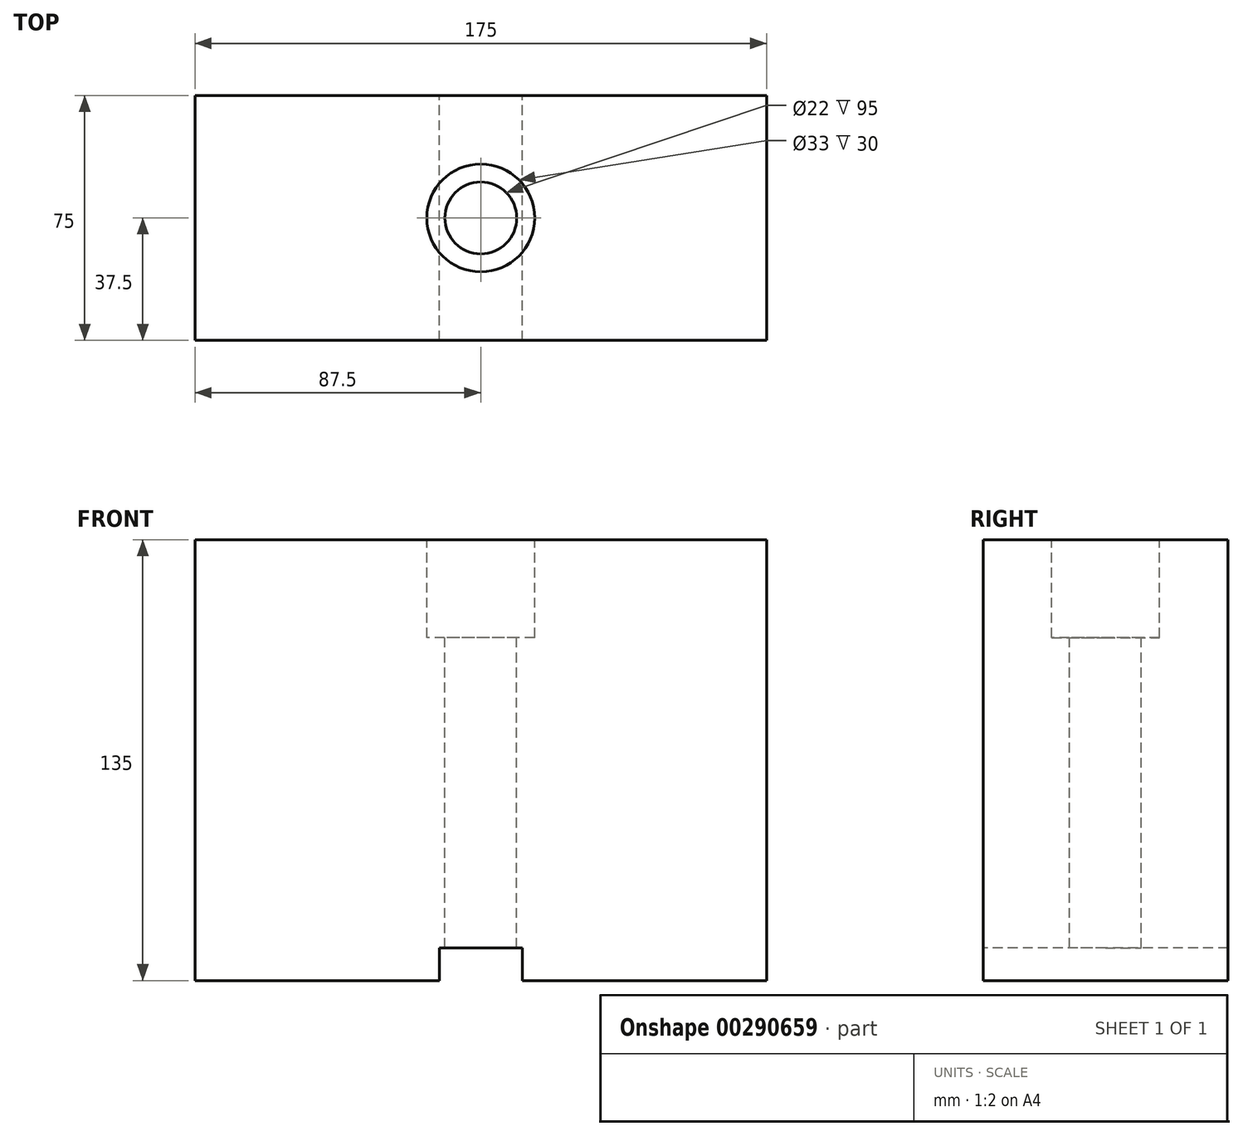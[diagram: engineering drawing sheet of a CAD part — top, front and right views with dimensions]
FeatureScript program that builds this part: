
annotation { "Feature Type Name" : "Feature", "Feature Type Description" : "" }
export const myFeature = defineFeature(function(context is Context, id is Id, definition is map)
    precondition{}
    {
        {
            var Q0;
            Q0=qCreatedBy(makeId("Front.planeOp"),FACE);
            var sketch = newSketch(context, id + "F0", { "sketchPlane" : qUnion([Q0])});
            skLineSegment(sketch, "E0.bottom", {"start": v(0, 0) * mm, "end": v(-175, 0) * mm});
            skLineSegment(sketch, "E0.top", {"start": v(0, 135) * mm, "end": v(-175, 135) * mm});
            skLineSegment(sketch, "E0.left", {"start": v(0, 0) * mm, "end": v(0, 135) * mm});
            skLineSegment(sketch, "E0.right", {"start": v(-175, 0) * mm, "end": v(-175, 135) * mm});
            skSolve(sketch);
        }
        {
            var Q0;
            Q0 = qSketchRegion(id + "F0", true);
            extrude(context, id + "F1", {"entities" : qUnion([Q0]), "depth" : 75 * mm});
        }
        {
            var Q0;
            Q0=makeQuery(id+"F1.opExtrude","CAP_FACE",FACE,{"disambiguationData":[OSD([sQuery(id+"F0.wireOp",EDGE,"E0.bottom"),sQuery(id+"F0.wireOp",EDGE,"E0.top"),sQuery(id+"F0.wireOp",EDGE,"E0.left"),sQuery(id+"F0.wireOp",EDGE,"E0.right")])],"isStart":false});
            var sketch = newSketch(context, id + "F2", { "sketchPlane" : qUnion([Q0])});
            skLineSegment(sketch, "E1.bottom", {"start": v(-100.2, 10) * mm, "end": v(-74.8, 10) * mm});
            skLineSegment(sketch, "E1.top", {"start": v(-100.2, -10) * mm, "end": v(-74.8, -10) * mm});
            skLineSegment(sketch, "E1.left", {"start": v(-100.2, 10) * mm, "end": v(-100.2, -10) * mm});
            skLineSegment(sketch, "E1.right", {"start": v(-74.8, 10) * mm, "end": v(-74.8, -10) * mm});
            skPoint(sketch, "E1.middle", {"position": v(-87.5, 0) * mm});
            skLineSegment(sketch, "E2", {"start": v(-87.5, 135) * mm, "end": v(-87.5, -32.02) * mm});
            skSolve(sketch);
        }
        {
            var Q0;
            Q0 = qSketchRegion(id + "F2", true);
            extrude(context, id + "F3", {"entities" : qUnion([Q0]), "operationType" : NewBodyOperationType.REMOVE, "oppositeDirection" : true, "depth" : 92.1 * mm});
        }
        {
            var Q0;
            Q0=makeQuery(id+"F1.opExtrude","SWEPT_FACE",FACE,{"disambiguationData":[OSD([sQuery(id+"F0.wireOp",EDGE,"E0.top")])]});
            var sketch = newSketch(context, id + "F4", { "sketchPlane" : qUnion([Q0])});
            skLineSegment(sketch, "E3", {"start": v(-175, -37.5) * mm, "end": v(0, -37.5) * mm});
            skLineSegment(sketch, "E4", {"start": v(-87.5, 0) * mm, "end": v(-87.5, -75) * mm});
            skPoint(sketch, "E5", {"position": v(-87.5, -37.5) * mm});
            skSolve(sketch);
        }
        {
            var Q0;
            Q0=sQuery(id+"F4.wireOp",VERTEX,"E5");
            var Q1;
            Q1=makeQuery(id+"F1.opExtrude","SWEPT_BODY",BODY,{"disambiguationData":[OSD([sQuery(id+"F0.wireOp",EDGE,"E0.bottom"),sQuery(id+"F0.wireOp",EDGE,"E0.top"),sQuery(id+"F0.wireOp",EDGE,"E0.left"),sQuery(id+"F0.wireOp",EDGE,"E0.right")])]});
            hole(context, id + "F5", {"style" : HoleStyle.C_BORE, "endStyle" : HoleEndStyle.BLIND, "holeDiameter" : 22 * mm, "cBoreDiameter" : 33 * mm, "cBoreDepth" : 30 * mm, "holeDepth" : 180 * mm, "tappedDepth" : 12 * mm, "tapClearance" : 3, "locations" : qUnion([Q0]), "scope" : qUnion([Q1])});
        }
    });
